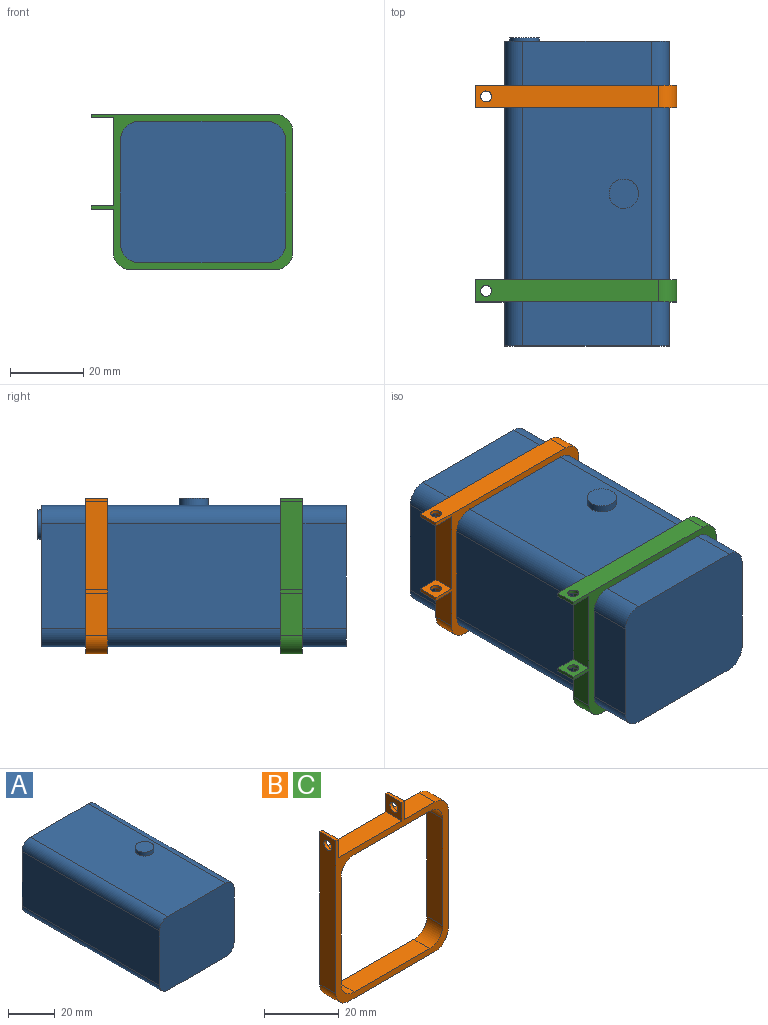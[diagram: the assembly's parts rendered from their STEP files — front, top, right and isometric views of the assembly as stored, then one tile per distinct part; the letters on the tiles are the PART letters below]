
ASSEMBLY  parts=3 mates=2
PART A: 14 faces, bbox 45x84x40.5 mm
  f0: plane 45x38.5mm, normal (0,1,0), area 1660.8mm2, adj f1,f2,f3,f4,f5,f6,f7,f8
  f1: cylinder r=5mm len=83mm, axis (0,1,0), area 651.9mm2, adj f0,f2,f8,f9
  f2: plane 83x28.5mm, normal (1,0,0), area 2365.5mm2, adj f0,f1,f3,f9
  f3: cylinder r=5mm len=83mm, axis (0,1,0), area 651.9mm2, adj f0,f2,f4,f9
  f4: plane 83x35mm, normal (0,0,-1), area 2905mm2, adj f0,f3,f5,f9
  f5: cylinder r=5mm len=83mm, axis (0,1,0), area 651.9mm2, adj f0,f4,f6,f9
  f6: plane 83x28.5mm, normal (-1,0,0), area 2365.5mm2, adj f0,f5,f7,f9
  f7: cylinder r=5mm len=83mm, axis (0,1,0), area 651.9mm2, adj f0,f6,f8,f9
  f8: plane 83x35mm, normal (0,0,1), area 2854.7mm2, adj f0,f1,f7,f9,f10
  f9: plane 45x38.5mm, normal (0,-1,0), area 1711mm2, adj f1,f2,f3,f4,f5,f6,f7,f8
  f10: cylinder r=4mm len=8mm, axis (0,0,1), area 50.3mm2, adj f8,f11
  f11: plane 8x8mm, normal (0,0,1), area 50.3mm2, adj f10
  f12: cylinder r=4mm len=8mm, axis (0,1,0), area 25.1mm2, adj f0,f13
  f13: plane 8x8mm, normal (0,1,0), area 50.3mm2, adj f12
PART B: 25 faces, bbox 42.5x6x55 mm
  f0: plane 55x42.5mm, normal (0,1,0), area 367.4mm2, adj f1,f2,f3,f4,f5,f6,f7,f8
  f1: plane 35x6mm, normal (1,0,0), area 210mm2, adj f0,f2,f8,f9
  f2: cylinder r=5mm len=6mm, axis (0,-1,0), area 47.1mm2, adj f0,f1,f3,f9
  f3: plane 28.5x6mm, normal (0,0,1), area 171mm2, adj f0,f2,f4,f9
  f4: cylinder r=5mm len=6mm, axis (0,-1,0), area 47.1mm2, adj f0,f3,f5,f9
  f5: plane 35x6mm, normal (-1,0,0), area 210mm2, adj f0,f4,f6,f9
  f6: cylinder r=5mm len=6mm, axis (0,-1,0), area 47.1mm2, adj f0,f5,f7,f9
  f7: plane 28.5x6mm, normal (0,0,-1), area 171mm2, adj f0,f6,f8,f9
  f8: cylinder r=5mm len=6mm, axis (0,-1,0), area 47.1mm2, adj f0,f1,f7,f9
  f9: plane 55x42.5mm, normal (0,-1,0), area 367.4mm2, adj f1,f2,f3,f4,f5,f6,f7,f8
  f10: plane 24x6mm, normal (0,0,1), area 144mm2, adj f0,f9,f11,f22
  f11: plane 6x6mm, normal (-1,0,0), area 28.9mm2, adj f0,f9,f10,f12,f24
  f12: plane 6x1mm, normal (0,0,1), area 6mm2, adj f0,f9,f11,f13
  f13: plane 6x6mm, normal (1,0,0), area 28.9mm2, adj f0,f9,f12,f14,f24
  f14: plane 11.5x6mm, normal (0,0,1), area 69mm2, adj f0,f9,f13,f15
  f15: cylinder r=5mm len=6mm, axis (0,1,0), area 47.1mm2, adj f0,f9,f14,f16
  f16: plane 39x6mm, normal (1,0,0), area 234mm2, adj f0,f9,f15,f17
  f17: cylinder r=5mm len=6mm, axis (0,1,0), area 47.1mm2, adj f0,f9,f16,f18
  f18: plane 32.5x6mm, normal (0,0,-1), area 195mm2, adj f0,f9,f17,f19
  f19: cylinder r=5mm len=6mm, axis (0,1,0), area 47.1mm2, adj f0,f9,f18,f20
  f20: plane 50x6mm, normal (-1,0,0), area 292.9mm2, adj f0,f9,f19,f21,f23
  f21: plane 6x1mm, normal (0,0,1), area 6mm2, adj f0,f9,f20,f22
  f22: plane 6x6mm, normal (1,0,0), area 28.9mm2, adj f0,f9,f10,f21,f23
  f23: cylinder r=1.5mm len=3mm, axis (1,0,0), area 9.4mm2, adj f20,f22
  f24: cylinder r=1.5mm len=3mm, axis (1,0,0), area 9.4mm2, adj f11,f13
PART C: same geometry as B
PLACE A rot(axis=(0.16,-0.06,-0.99),0deg) t=(-45.06,69.13,-14.47)mm fixed
PLACE B rot(axis=(-0.71,0,0.71),180deg) t=(-39.56,51.13,-33.47)mm
PLACE C rot(axis=(-0.71,0,0.71),180deg) t=(-39.56,-1.87,-33.47)mm
MATE fastened A.f8 <-> B.f1  axis (0,0,1) through (-55.56,69.13,-33.47)mm
MATE fastened A.f8 <-> C.f1  axis (0,0,1) through (-55.56,-13.87,-33.47)mm
